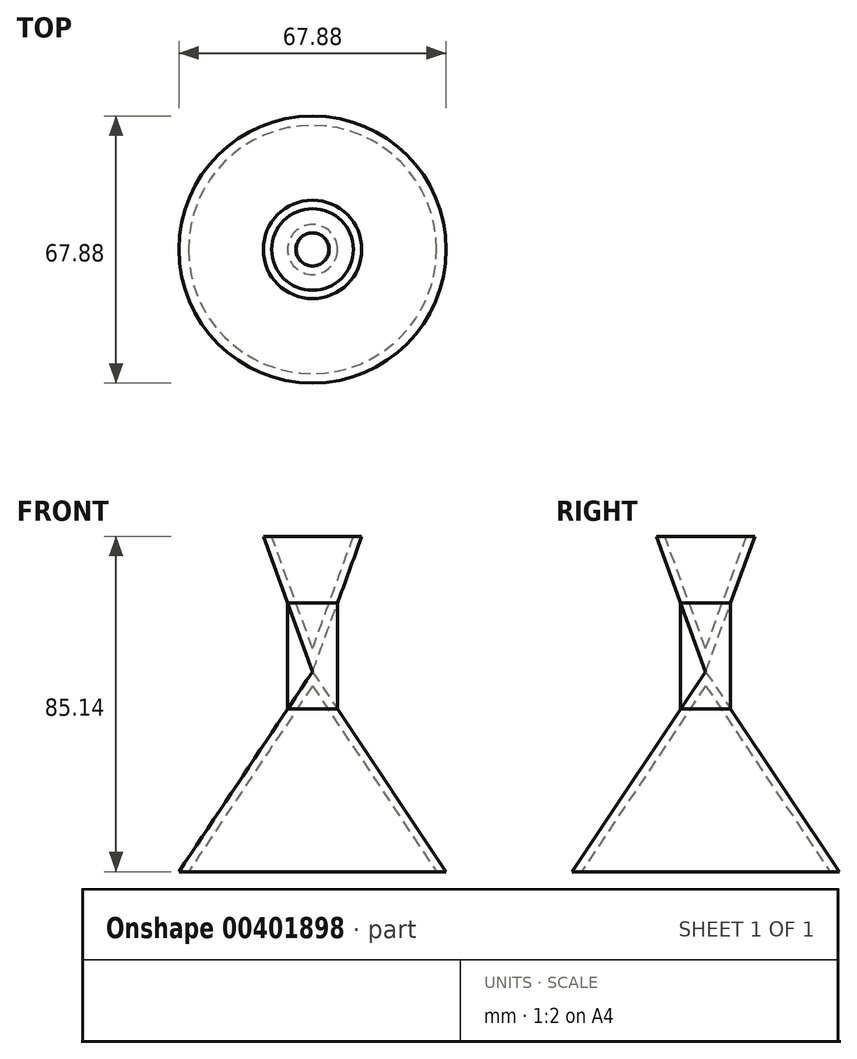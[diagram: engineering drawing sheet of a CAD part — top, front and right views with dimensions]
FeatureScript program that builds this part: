
annotation { "Feature Type Name" : "Feature", "Feature Type Description" : "" }
export const myFeature = defineFeature(function(context is Context, id is Id, definition is map)
    precondition{}
    {
        {
            var Q0;
            Q0=qCreatedBy(makeId("Front.planeOp"),FACE);
            var sketch = newSketch(context, id + "F0", { "sketchPlane" : qUnion([Q0])});
            skLineSegment(sketch, "E0", {"start": v(0, 0) * mm, "end": v(-12.5, 34.34) * mm});
            skLineSegment(sketch, "E1.MirrorCS", {"start": v(0, 0) * mm, "end": v(12.5, 34.34) * mm});
            skLineSegment(sketch, "E2", {"start": v(-12.5, 34.34) * mm, "end": v(12.5, 34.34) * mm});
            skLineSegment(sketch, "E3", {"start": v(0, 0) * mm, "end": v(-33.94, -50.8) * mm});
            skLineSegment(sketch, "E4.MirrorCS", {"start": v(0, 0) * mm, "end": v(33.94, -50.8) * mm});
            skLineSegment(sketch, "E5", {"start": v(-33.94, -50.8) * mm, "end": v(33.94, -50.8) * mm});
            skLineSegment(sketch, "E6", {"start": v(0, 34.34) * mm, "end": v(0, -50.8) * mm});
            skLineSegment(sketch, "E7", {"start": v(-6.35, 17.45) * mm, "end": v(-6.35, -9.5) * mm});
            skLineSegment(sketch, "E8.MirrorCS", {"start": v(6.35, 17.45) * mm, "end": v(6.35, -9.5) * mm});
            skLineSegment(sketch, "E9", {"start": v(10.37, 34.34) * mm, "end": v(0, 5.85) * mm});
            skLineSegment(sketch, "E10.MirrorCS", {"start": v(-10.37, 34.34) * mm, "end": v(0, 5.85) * mm});
            skLineSegment(sketch, "E11", {"start": v(-31.54, -50.8) * mm, "end": v(0, -3.6) * mm});
            skLineSegment(sketch, "E12.MirrorCS", {"start": v(31.54, -50.8) * mm, "end": v(0, -3.6) * mm});
            skLineSegment(sketch, "E13", {"start": v(-6.35, -9.5) * mm, "end": v(6.35, -9.5) * mm});
            skLineSegment(sketch, "E14", {"start": v(-6.35, 17.45) * mm, "end": v(6.35, 17.45) * mm});
            skSolve(sketch);
        }
        {
            var Q0;
            {var subQ6=sQuery(id+"F0.wireOp",EDGE,"E9");Q0=makeQuery(id+"F0.imprint","IMPRINT",FACE,{"disambiguationData":[TD([[makeQuery(id+"F0.imprint","IMPRINT",EDGE,{"derivedFrom":subQ6}),1.0]])]});}
            var Q1;
            Q1=sQuery(id+"F0.wireOp",EDGE,"E6");
            revolve(context, id + "F1", {"entities" : qUnion([Q0]), "axis" : qUnion([Q1]), "revolveType" : RevolveType.FULL});
        }
        {
            var Q0;
            {var subQ3=sQuery(id+"F0.wireOp",EDGE,"E11");Q0=makeQuery(id+"F0.imprint","IMPRINT",FACE,{"disambiguationData":[TD([[makeQuery(id+"F0.imprint","IMPRINT",EDGE,{"derivedFrom":subQ3}),1.0]])]});}
            var Q1;
            Q1=sQuery(id+"F0.wireOp",EDGE,"E6");
            revolve(context, id + "F2", {"entities" : qUnion([Q0]), "axis" : qUnion([Q1]), "revolveType" : RevolveType.FULL});
        }
        {
            var Q0;
            {var subQ3=sQuery(id+"F0.wireOp",EDGE,"E8.MirrorCS");Q0=makeQuery(id+"F0.imprint","IMPRINT",FACE,{"disambiguationData":[TD([[makeQuery(id+"F0.imprint","IMPRINT",EDGE,{"derivedFrom":subQ3}),-1.0]])]});}
            var Q1;
            {var subQ3=sQuery(id+"F0.wireOp",EDGE,"E14");var subQ5=sQuery(id+"F0.wireOp",EDGE,"E9");var subQ7=makeQuery(id+"F0.imprint","INTERSECT",VERTEX,{"derivedFrom":[subQ5,subQ3]});Q1=makeQuery(id+"F0.imprint","IMPRINT",FACE,{"disambiguationData":[TD([[makeQuery(id+"F0.imprint","IMPRINT",EDGE,{"disambiguationData":[TD([[subQ7,-1.0]])],"derivedFrom":subQ5}),1.0]])]});}
            var Q2;
            {var subQ3=sQuery(id+"F0.wireOp",EDGE,"E13");var subQ5=sQuery(id+"F0.wireOp",EDGE,"E12.MirrorCS");var subQ6=makeQuery(id+"F0.imprint","INTERSECT",VERTEX,{"derivedFrom":[subQ5,subQ3]});Q2=makeQuery(id+"F0.imprint","IMPRINT",FACE,{"disambiguationData":[TD([[makeQuery(id+"F0.imprint","IMPRINT",EDGE,{"disambiguationData":[TD([[subQ6,-1.0]])],"derivedFrom":subQ5}),-1.0]])]});}
            var Q3;
            Q3=sQuery(id+"F0.wireOp",EDGE,"E6");
            revolve(context, id + "F3", {"entities" : qUnion([Q0, Q1, Q2]), "axis" : qUnion([Q3]), "revolveType" : RevolveType.FULL});
        }
    });
